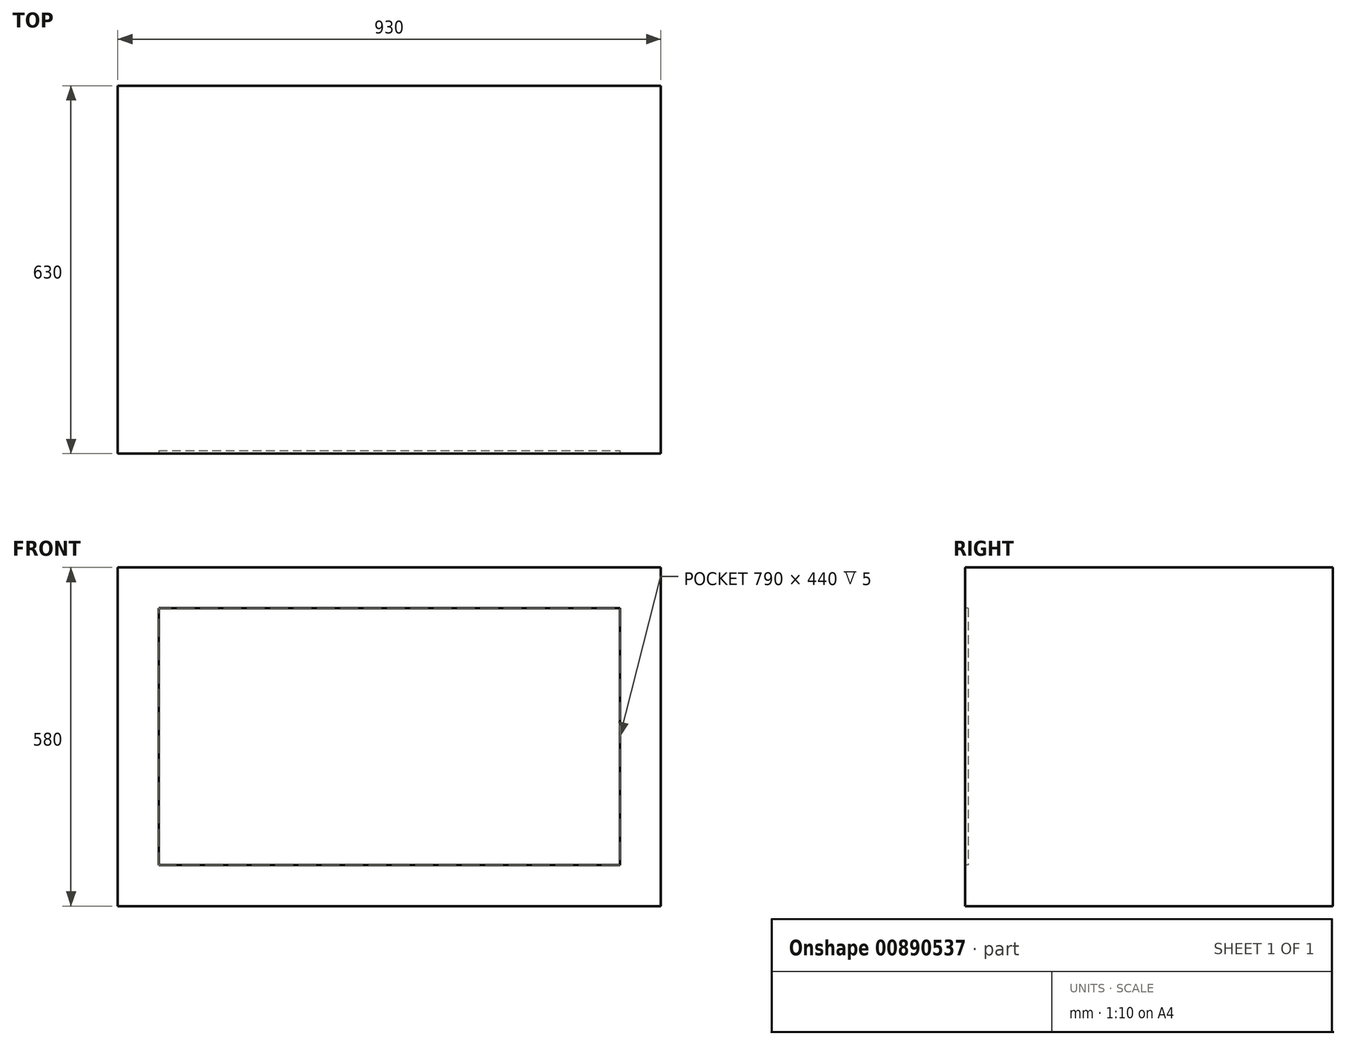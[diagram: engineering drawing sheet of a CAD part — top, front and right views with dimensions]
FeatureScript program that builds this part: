
annotation { "Feature Type Name" : "Feature", "Feature Type Description" : "" }
export const myFeature = defineFeature(function(context is Context, id is Id, definition is map)
    precondition{}
    {
        {
            var Q0;
            Q0=qCreatedBy(makeId("Top.planeOp"),FACE);
            var sketch = newSketch(context, id + "F0", { "sketchPlane" : qUnion([Q0])});
            skLineSegment(sketch, "E0.bottom", {"start": v(465, 315) * mm, "end": v(-465, 315) * mm});
            skLineSegment(sketch, "E0.top", {"start": v(465, -315) * mm, "end": v(-465, -315) * mm});
            skLineSegment(sketch, "E0.left", {"start": v(465, 315) * mm, "end": v(465, -315) * mm});
            skLineSegment(sketch, "E0.right", {"start": v(-465, 315) * mm, "end": v(-465, -315) * mm});
            skPoint(sketch, "E0.middle", {"position": v(0, 0) * mm});
            skSolve(sketch);
        }
        {
            var Q0;
            Q0=makeQuery(id+"F0.imprint","IMPRINT",FACE,{"disambiguationData":[TD([[makeQuery(id+"F0.imprint","IMPRINT",EDGE,{"derivedFrom":sQuery(id+"F0.wireOp",EDGE,"E0.bottom")}),1.0]])]});
            extrude(context, id + "F1", {"entities" : qUnion([Q0]), "depth" : 580 * mm, "offsetDistance" : 25 * mm});
        }
        {
            var Q0;
            Q0=makeQuery(id+"F1.opExtrude","SWEPT_FACE",FACE,{"disambiguationData":[OSD([sQuery(id+"F0.wireOp",EDGE,"E0.top")])]});
            var sketch = newSketch(context, id + "F2", { "sketchPlane" : qUnion([Q0])});
            skLineSegment(sketch, "E1.0", {"start": v(-395, 70) * mm, "end": v(395, 70) * mm});
            skLineSegment(sketch, "E1.1", {"start": v(-395, 510) * mm, "end": v(-395, 70) * mm});
            skLineSegment(sketch, "E1.2", {"start": v(395, 510) * mm, "end": v(-395, 510) * mm});
            skLineSegment(sketch, "E1.3", {"start": v(395, 70) * mm, "end": v(395, 510) * mm});
            skSolve(sketch);
        }
        {
            var Q0;
            Q0=makeQuery(id+"F2.imprint","IMPRINT",FACE,{"disambiguationData":[TD([[makeQuery(id+"F2.imprint","IMPRINT",EDGE,{"derivedFrom":sQuery(id+"F2.wireOp",EDGE,"E1.0")}),1.0]])]});
            extrude(context, id + "F3", {"entities" : qUnion([Q0]), "operationType" : NewBodyOperationType.REMOVE, "oppositeDirection" : true, "depth" : 5 * mm, "offsetDistance" : 25 * mm});
        }
    });
